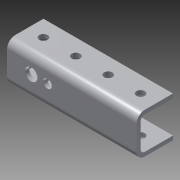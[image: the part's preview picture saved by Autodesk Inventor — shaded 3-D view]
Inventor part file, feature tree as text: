
AUTODESK INVENTOR PART (.ipt)
format: ipt  version: 2014 SP1 (Build 180222100, 222)  size: 187,392 bytes
history: native  units: in
note: dims shown in document units (in); Inventor stores cm internally (conversion verified against a paired STEP export)
features: sketch x5, extrude x3, hole x3, pattern_linear x1
ambient origin geometry x8: Origin, YZ Plane, XZ Plane, XY Plane, X Axis, Y Axis, Z Axis, Center Point
bodies: Solid1 (feature_tree)
feature tree (12):
  extrude  "Extrusion1"  Depth=0.125in
  sketch  "Sketch2"  dims[d2=1.0in d3=1.0in]
  hole  "Hole1"  [1 undecoded]
  hole  "Hole2"  [1 undecoded]
  hole  "Hole3"  [1 undecoded]
  pattern_linear  "Rectangular Pattern1"  Spacing1=0.15in  [1 undecoded]
  extrude  "Extrusion2"  Depth=0.3937in
  extrude  "Extrusion3"  Depth=1.0in
  sketch  "Sketch1"  dims[d0=1.125in d1=0.125in]
  sketch  "Sketch3"  dims[d4=0.125in d5=0.125in]
  sketch  "Sketch4"  dims[d6=0.25in d7=35.0in d8=0.0in]
  sketch  "Sketch5"  dims[d10=0.3in d11=0.15in d12=0.7874in d14=10.0in d15=0.3937in d17=1.0in d20=0.38in d21=0.75in d22=0.375in d23=0.25in d24=0.5635in d25=1.0in d26=0.8108in d27=0.125in d28=0.75in d29=0.375in d30=0.25in d31=0.5635in d32=1.0in d33=0.8108in d34=0.5in d35=0.5in d36=0.257in d37=0.75in d38=0.375in d39=0.25in d40=0.5635in d41=1.0in d42=0.8108in d43=13.7795in d45=1.0in d46=31.0in d47=0.0in d48=0.266in d49=0.5in d50=1.0in d51=0.0in]
note: 4 required parameter values undecoded (feature->parameter linkage not recoverable at this tier; creation-order binding heuristic only, values carry confidence <= 0.55)
